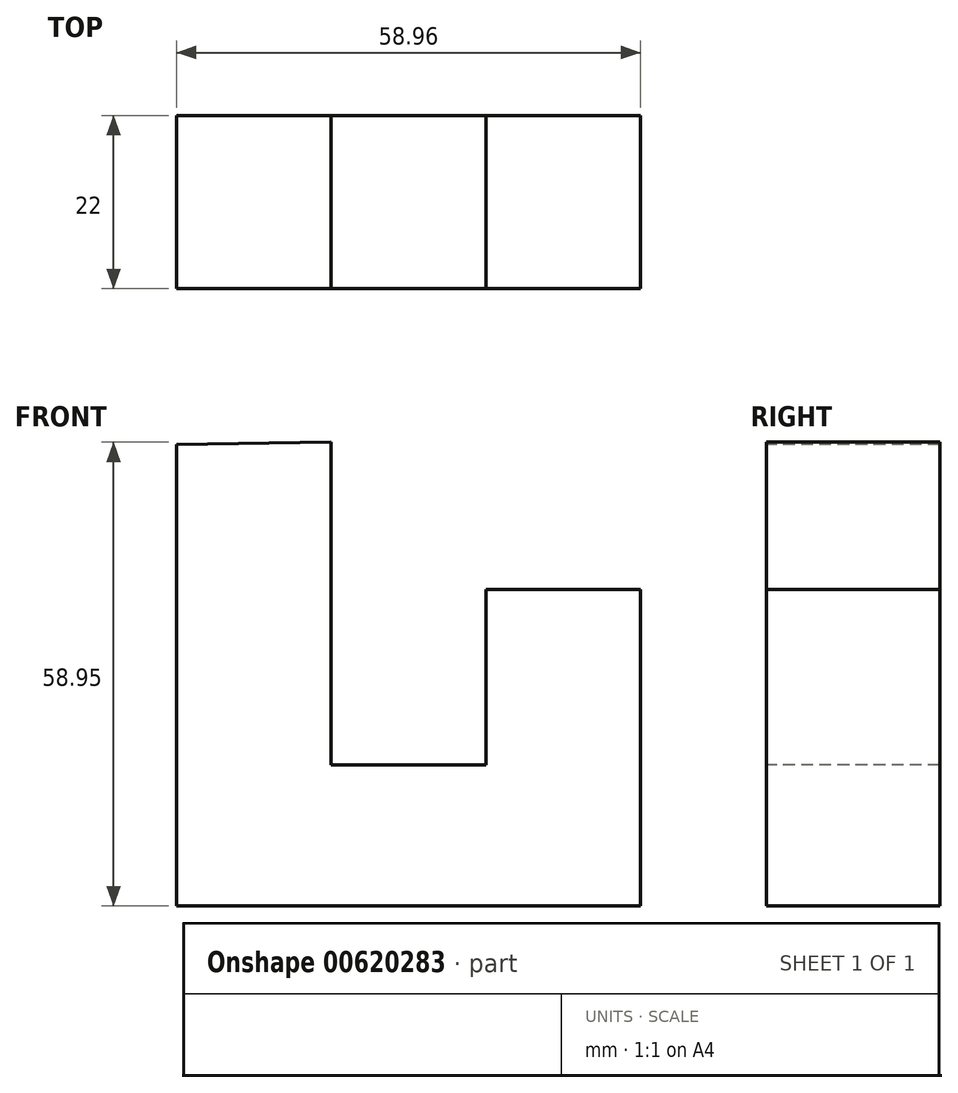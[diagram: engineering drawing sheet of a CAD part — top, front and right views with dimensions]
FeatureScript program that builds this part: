
annotation { "Feature Type Name" : "Feature", "Feature Type Description" : "" }
export const myFeature = defineFeature(function(context is Context, id is Id, definition is map)
    precondition{}
    {
        {
            var Q0;
            Q0=qCreatedBy(makeId("Front.planeOp"),FACE);
            var sketch = newSketch(context, id + "F0", { "sketchPlane" : qUnion([Q0])});
            skLineSegment(sketch, "E0", {"start": v(-58.96, 40.7) * mm, "end": v(-58.96, -17.96) * mm});
            skLineSegment(sketch, "E1", {"start": v(-58.96, -17.96) * mm, "end": v(0, -17.96) * mm});
            skLineSegment(sketch, "E2", {"start": v(0, -17.96) * mm, "end": v(0, 22.3) * mm});
            skLineSegment(sketch, "E3", {"start": v(0, 22.3) * mm, "end": v(-19.62, 22.3) * mm});
            skLineSegment(sketch, "E4", {"start": v(-19.62, 22.3) * mm, "end": v(-19.62, 0) * mm});
            skLineSegment(sketch, "E5", {"start": v(-19.62, 0) * mm, "end": v(-39.34, 0) * mm});
            skLineSegment(sketch, "E6", {"start": v(-39.34, 0) * mm, "end": v(-39.34, 41) * mm});
            skLineSegment(sketch, "E7", {"start": v(-39.34, 41) * mm, "end": v(-58.96, 40.7) * mm});
            skSolve(sketch);
        }
        {
            var Q0;
            Q0 = qSketchRegion(id + "F0", true);
            extrude(context, id + "F1", {"entities" : qUnion([Q0]), "oppositeDirection" : true, "depth" : 22 * mm, "offsetDistance" : 25 * mm});
        }
    });
